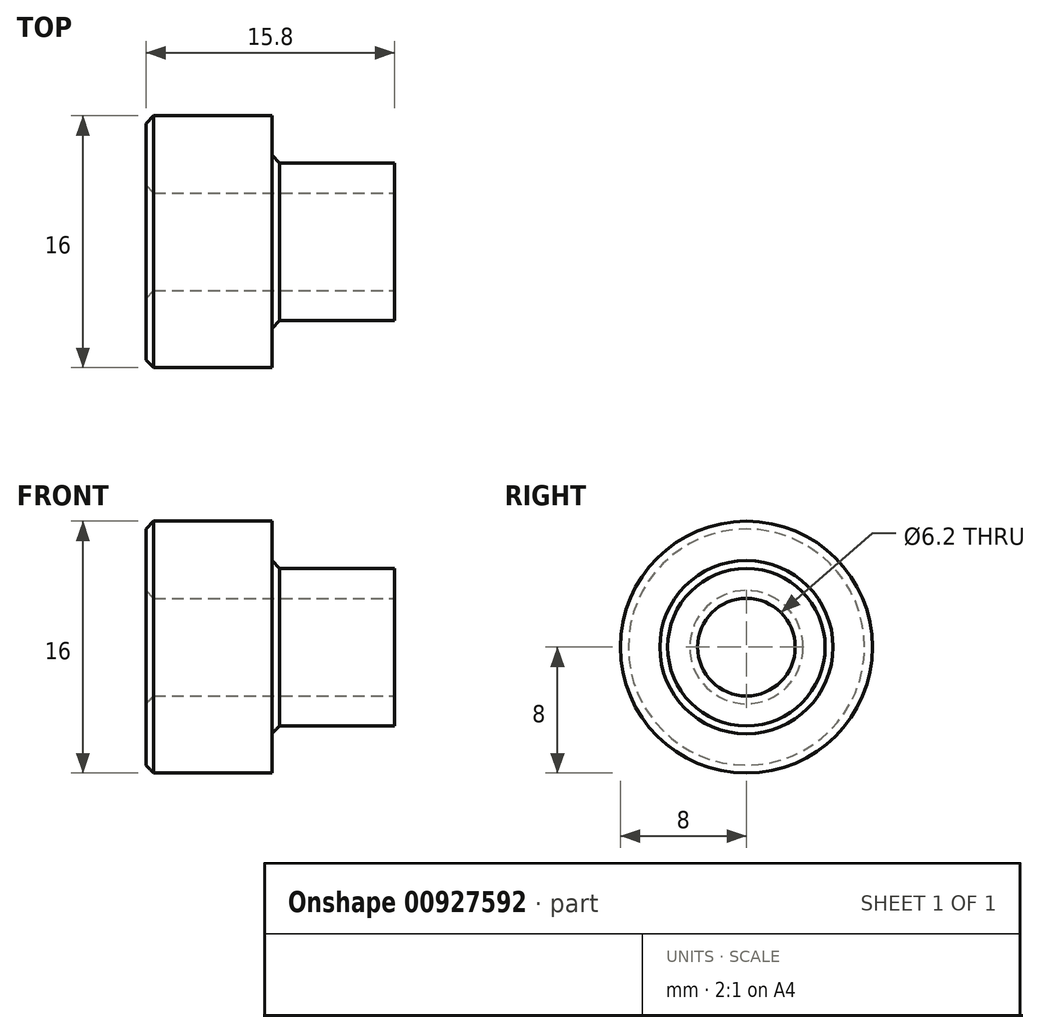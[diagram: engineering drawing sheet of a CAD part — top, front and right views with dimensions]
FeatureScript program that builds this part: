
annotation { "Feature Type Name" : "Feature", "Feature Type Description" : "" }
export const myFeature = defineFeature(function(context is Context, id is Id, definition is map)
    precondition{}
    {
        {
            var Q0;
            Q0=qCreatedBy(makeId("Right.planeOp"),FACE);
            var sketch = newSketch(context, id + "F0", { "sketchPlane" : qUnion([Q0])});
            skCircle(sketch, "E0", {"center": v(0, 0) * mm, "radius": 8 * mm});
            skSolve(sketch);
        }
        {
            var Q0;
            Q0 = qSketchRegion(id + "F0", true);
            extrude(context, id + "F1", {"entities" : qUnion([Q0]), "oppositeDirection" : true, "depth" : 15.8 * mm, "offsetDistance" : 25 * mm});
        }
        {
            var Q0;
            Q0=makeQuery(id+"F1.opExtrude","CAP_FACE",FACE,{"disambiguationData":[OSD([sQuery(id+"F0.wireOp",EDGE,"E0")])],"isStart":true});
            var sketch = newSketch(context, id + "F2", { "sketchPlane" : qUnion([Q0])});
            skCircle(sketch, "E1", {"center": v(0, 0) * mm, "radius": 5 * mm});
            skSolve(sketch);
        }
        {
            var Q0;
            Q0=makeQuery(id+"F2.imprint","IMPRINT",FACE,{"disambiguationData":[TD([[makeQuery(id+"F2.imprint","IMPRINT",EDGE,{"derivedFrom":sQuery(id+"F2.wireOp",EDGE,"E1")}),-1.0]])]});
            extrude(context, id + "F3", {"entities" : qUnion([Q0]), "operationType" : NewBodyOperationType.REMOVE, "oppositeDirection" : true, "depth" : 7.8 * mm, "offsetDistance" : 25 * mm});
        }
        {
            var Q0;
            Q0=makeQuery(id+"F1.opExtrude","CAP_FACE",FACE,{"disambiguationData":[OSD([sQuery(id+"F0.wireOp",EDGE,"E0")])],"isStart":true});
            var sketch = newSketch(context, id + "F4", { "sketchPlane" : qUnion([Q0])});
            skCircle(sketch, "E2", {"center": v(0, 0) * mm, "radius": 3.1 * mm});
            skSolve(sketch);
        }
        {
            var Q0;
            Q0 = qSketchRegion(id + "F4", true);
            extrude(context, id + "F5", {"entities" : qUnion([Q0]), "operationType" : NewBodyOperationType.REMOVE, "oppositeDirection" : true, "depth" : 25 * mm, "offsetDistance" : 25 * mm});
        }
        {
            var Q0;
            Q0=makeQuery(id+"F5.boolean.opBoolean","COPY",EDGE,{"derivedFrom":makeQuery(id+"F5.opExtrude","CAP_EDGE",EDGE,{"disambiguationData":[OSD([sQuery(id+"F4.wireOp",EDGE,"E2")])],"isStart":true})});
            var Q1;
            Q1=makeQuery(id+"F5.boolean.opBoolean","INTERSECT",EDGE,{"derivedFrom":[makeQuery(id+"F1.opExtrude","CAP_FACE",FACE,{"disambiguationData":[OSD([sQuery(id+"F0.wireOp",EDGE,"E0")])],"isStart":false}),makeQuery(id+"F5.opExtrude","SWEPT_FACE",FACE,{"disambiguationData":[OSD([sQuery(id+"F4.wireOp",EDGE,"E2")])]})]});
            var Q2;
            Q2=makeQuery(id+"F3.boolean.opBoolean","COPY",EDGE,{"derivedFrom":makeQuery(id+"F3.opExtrude","CAP_EDGE",EDGE,{"disambiguationData":[OSD([sQuery(id+"F2.wireOp",EDGE,"E1")])],"isStart":true})});
            var Q3;
            Q3=makeQuery(id+"F3.boolean.opBoolean","COPY",EDGE,{"derivedFrom":makeQuery(id+"F3.opExtrude","CAP_EDGE",EDGE,{"disambiguationData":[OSD([sQuery(id+"F2.wireOp",EDGE,"E1")])],"isStart":false})});
            var Q4;
            Q4=makeQuery(id+"F3.boolean.opBoolean","COPY",EDGE,{"derivedFrom":makeQuery(id+"F3.opExtrude","CAP_EDGE",EDGE,{"disambiguationData":[OSD([sQuery(id+"F0.wireOp",EDGE,"E0")])],"isStart":false})});
            var Q5;
            Q5=makeQuery(id+"F1.opExtrude","CAP_EDGE",EDGE,{"disambiguationData":[OSD([sQuery(id+"F0.wireOp",EDGE,"E0")])],"isStart":false});
            chamfer(context, id + "F6", {"entities" : qUnion([Q0, Q1, Q2, Q3, Q4, Q5]), "width" : 0.5 * mm, "tangentPropagation" : true});
        }
    });
